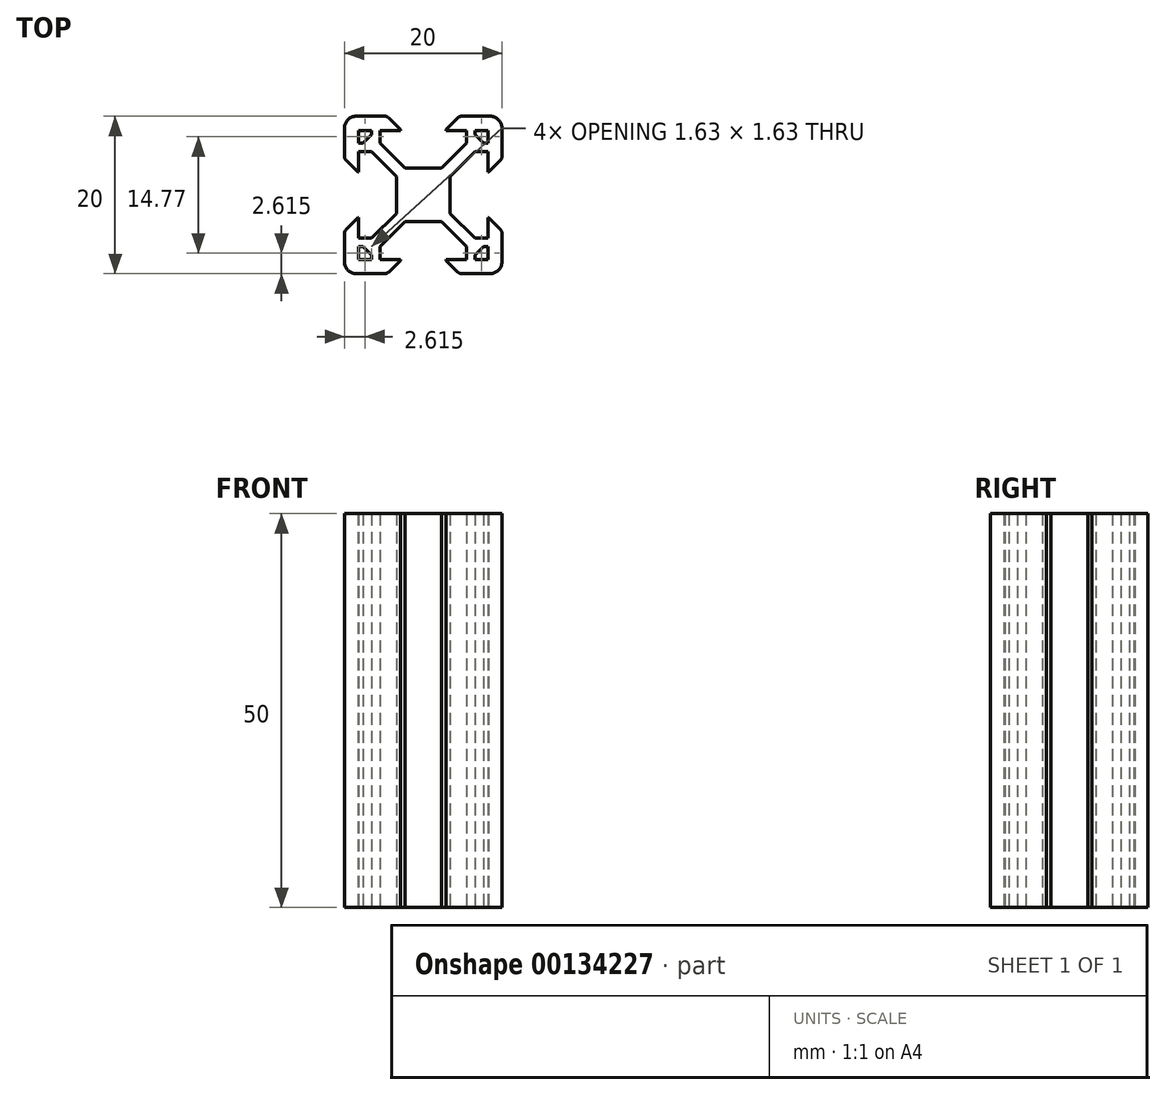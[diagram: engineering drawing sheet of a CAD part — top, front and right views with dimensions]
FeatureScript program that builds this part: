
annotation { "Feature Type Name" : "Feature", "Feature Type Description" : "" }
export const myFeature = defineFeature(function(context is Context, id is Id, definition is map)
    precondition{}
    {
        {
            var Q0;
            Q0=qCreatedBy(makeId("Top.planeOp"),FACE);
            var sketch = newSketch(context, id + "F0", { "sketchPlane" : qUnion([Q0])});
            skLineSegment(sketch, "E0.0.0", {"start": v(-6.56, 5.5) * mm, "end": v(-3.4, 2.34) * mm});
            skLineSegment(sketch, "E0.0.1", {"start": v(-3.4, 2.34) * mm, "end": v(-3.4, -2.34) * mm});
            skLineSegment(sketch, "E0.0.2", {"start": v(-3.4, -2.34) * mm, "end": v(-6.56, -5.5) * mm});
            skLineSegment(sketch, "E0.0.3", {"start": v(-6.56, -5.5) * mm, "end": v(-8.2, -5.5) * mm});
            skLineSegment(sketch, "E0.0.4", {"start": v(-8.2, -5.5) * mm, "end": v(-8.2, -2.9) * mm});
            skLineSegment(sketch, "E0.0.5", {"start": v(-8.2, -2.9) * mm, "end": v(-8.3, -2.9) * mm});
            skLineSegment(sketch, "E0.0.6", {"start": v(-8.3, -2.9) * mm, "end": v(-9.77, -4.35) * mm});
            skArc(sketch, "E0.0.7", {"start": v(-9.77, -4.35) * mm, "mid": v(-9.94, -4.6) * mm, "end": v(-10, -4.9) * mm});
            skLineSegment(sketch, "E0.0.8", {"start": v(-10, -4.9) * mm, "end": v(-10, -8.5) * mm});
            skArc(sketch, "E0.0.9", {"start": v(-10, -8.5) * mm, "mid": v(-9.56, -9.56) * mm, "end": v(-8.5, -10) * mm});
            skLineSegment(sketch, "E0.0.10", {"start": v(-8.5, -10) * mm, "end": v(-4.9, -10) * mm});
            skArc(sketch, "E0.0.11", {"start": v(-4.9, -10) * mm, "mid": v(-4.6, -9.94) * mm, "end": v(-4.35, -9.77) * mm});
            skLineSegment(sketch, "E0.0.12", {"start": v(-4.35, -9.77) * mm, "end": v(-2.89, -8.31) * mm});
            skLineSegment(sketch, "E0.0.13", {"start": v(-2.9, -8.3) * mm, "end": v(-2.89, -8.2) * mm});
            skLineSegment(sketch, "E0.0.14", {"start": v(-2.9, -8.2) * mm, "end": v(-5.5, -8.2) * mm});
            skLineSegment(sketch, "E0.0.15", {"start": v(-5.5, -8.2) * mm, "end": v(-5.5, -6.56) * mm});
            skLineSegment(sketch, "E0.0.16", {"start": v(-5.5, -6.56) * mm, "end": v(-2.34, -3.4) * mm});
            skLineSegment(sketch, "E0.0.17", {"start": v(-2.34, -3.4) * mm, "end": v(2.34, -3.4) * mm});
            skLineSegment(sketch, "E0.0.18", {"start": v(2.34, -3.4) * mm, "end": v(5.5, -6.56) * mm});
            skLineSegment(sketch, "E0.0.19", {"start": v(5.5, -6.56) * mm, "end": v(5.5, -8.2) * mm});
            skLineSegment(sketch, "E0.0.20", {"start": v(5.5, -8.2) * mm, "end": v(2.9, -8.2) * mm});
            skLineSegment(sketch, "E0.0.21", {"start": v(2.89, -8.2) * mm, "end": v(2.9, -8.3) * mm});
            skLineSegment(sketch, "E0.0.22", {"start": v(2.89, -8.3) * mm, "end": v(4.35, -9.77) * mm});
            skArc(sketch, "E0.0.23", {"start": v(4.35, -9.77) * mm, "mid": v(4.6, -9.94) * mm, "end": v(4.9, -10) * mm});
            skLineSegment(sketch, "E0.0.24", {"start": v(4.9, -10) * mm, "end": v(8.5, -10) * mm});
            skArc(sketch, "E0.0.25", {"start": v(8.5, -10) * mm, "mid": v(9.56, -9.56) * mm, "end": v(10, -8.5) * mm});
            skLineSegment(sketch, "E0.0.26", {"start": v(10, -8.5) * mm, "end": v(10, -4.9) * mm});
            skArc(sketch, "E0.0.27", {"start": v(10, -4.9) * mm, "mid": v(9.94, -4.6) * mm, "end": v(9.77, -4.35) * mm});
            skLineSegment(sketch, "E0.0.28", {"start": v(9.77, -4.35) * mm, "end": v(8.3, -2.9) * mm});
            skLineSegment(sketch, "E0.0.29", {"start": v(8.3, -2.9) * mm, "end": v(8.2, -2.9) * mm});
            skLineSegment(sketch, "E0.0.30", {"start": v(8.2, -2.9) * mm, "end": v(8.2, -5.5) * mm});
            skLineSegment(sketch, "E0.0.31", {"start": v(8.2, -5.5) * mm, "end": v(6.56, -5.5) * mm});
            skLineSegment(sketch, "E0.0.32", {"start": v(6.56, -5.5) * mm, "end": v(3.4, -2.34) * mm});
            skLineSegment(sketch, "E0.0.33", {"start": v(3.4, -2.34) * mm, "end": v(3.4, 2.34) * mm});
            skLineSegment(sketch, "E0.0.34", {"start": v(3.4, 2.34) * mm, "end": v(6.56, 5.5) * mm});
            skLineSegment(sketch, "E0.0.35", {"start": v(6.56, 5.5) * mm, "end": v(8.2, 5.5) * mm});
            skLineSegment(sketch, "E0.0.36", {"start": v(8.2, 5.5) * mm, "end": v(8.2, 2.9) * mm});
            skLineSegment(sketch, "E0.0.37", {"start": v(8.2, 2.9) * mm, "end": v(8.3, 2.9) * mm});
            skLineSegment(sketch, "E0.0.38", {"start": v(8.3, 2.9) * mm, "end": v(9.77, 4.35) * mm});
            skArc(sketch, "E0.0.39", {"start": v(9.77, 4.35) * mm, "mid": v(9.94, 4.6) * mm, "end": v(10, 4.9) * mm});
            skLineSegment(sketch, "E0.0.40", {"start": v(10, 4.9) * mm, "end": v(10, 8.5) * mm});
            skArc(sketch, "E0.0.41", {"start": v(10, 8.5) * mm, "mid": v(9.56, 9.56) * mm, "end": v(8.5, 10) * mm});
            skLineSegment(sketch, "E0.0.42", {"start": v(8.5, 10) * mm, "end": v(4.9, 10) * mm});
            skArc(sketch, "E0.0.43", {"start": v(4.9, 10) * mm, "mid": v(4.6, 9.94) * mm, "end": v(4.35, 9.77) * mm});
            skLineSegment(sketch, "E0.0.44", {"start": v(4.35, 9.77) * mm, "end": v(2.89, 8.3) * mm});
            skLineSegment(sketch, "E0.0.45", {"start": v(2.9, 8.3) * mm, "end": v(2.89, 8.2) * mm});
            skLineSegment(sketch, "E0.0.46", {"start": v(2.9, 8.2) * mm, "end": v(5.5, 8.2) * mm});
            skLineSegment(sketch, "E0.0.47", {"start": v(5.5, 8.2) * mm, "end": v(5.5, 6.56) * mm});
            skLineSegment(sketch, "E0.0.48", {"start": v(5.5, 6.56) * mm, "end": v(2.34, 3.4) * mm});
            skLineSegment(sketch, "E0.0.49", {"start": v(2.34, 3.4) * mm, "end": v(-2.34, 3.4) * mm});
            skLineSegment(sketch, "E0.0.50", {"start": v(-2.34, 3.4) * mm, "end": v(-5.5, 6.56) * mm});
            skLineSegment(sketch, "E0.0.51", {"start": v(-5.5, 6.56) * mm, "end": v(-5.5, 8.2) * mm});
            skLineSegment(sketch, "E0.0.52", {"start": v(-5.5, 8.2) * mm, "end": v(-2.9, 8.2) * mm});
            skLineSegment(sketch, "E0.0.53", {"start": v(-2.89, 8.2) * mm, "end": v(-2.9, 8.3) * mm});
            skLineSegment(sketch, "E0.0.54", {"start": v(-2.89, 8.31) * mm, "end": v(-4.35, 9.77) * mm});
            skArc(sketch, "E0.0.55", {"start": v(-4.35, 9.77) * mm, "mid": v(-4.6, 9.94) * mm, "end": v(-4.9, 10) * mm});
            skLineSegment(sketch, "E0.0.56", {"start": v(-4.9, 10) * mm, "end": v(-8.5, 10) * mm});
            skArc(sketch, "E0.0.57", {"start": v(-8.5, 10) * mm, "mid": v(-9.56, 9.56) * mm, "end": v(-10, 8.5) * mm});
            skLineSegment(sketch, "E0.0.58", {"start": v(-10, 8.5) * mm, "end": v(-10, 4.9) * mm});
            skArc(sketch, "E0.0.59", {"start": v(-10, 4.9) * mm, "mid": v(-9.94, 4.6) * mm, "end": v(-9.77, 4.35) * mm});
            skLineSegment(sketch, "E0.0.60", {"start": v(-9.77, 4.35) * mm, "end": v(-8.3, 2.9) * mm});
            skLineSegment(sketch, "E0.0.61", {"start": v(-8.3, 2.9) * mm, "end": v(-8.2, 2.9) * mm});
            skLineSegment(sketch, "E0.0.62", {"start": v(-8.2, 2.9) * mm, "end": v(-8.2, 5.5) * mm});
            skLineSegment(sketch, "E0.0.63", {"start": v(-8.2, 5.5) * mm, "end": v(-6.56, 5.5) * mm});
            skLineSegment(sketch, "E1.0", {"start": v(-6.57, 8.2) * mm, "end": v(-8.2, 8.2) * mm});
            skLineSegment(sketch, "E2.0", {"start": v(-8.2, 8.2) * mm, "end": v(-8.2, 6.57) * mm});
            skLineSegment(sketch, "E3.0", {"start": v(-6.57, 7.66) * mm, "end": v(-6.57, 8.2) * mm});
            skLineSegment(sketch, "E4.0", {"start": v(-7.66, 6.57) * mm, "end": v(-6.57, 7.66) * mm});
            skLineSegment(sketch, "E5.0", {"start": v(-8.2, 6.57) * mm, "end": v(-7.66, 6.57) * mm});
            skLineSegment(sketch, "E6.1.0", {"start": v(-6.57, -7.66) * mm, "end": v(-7.66, -6.57) * mm});
            skLineSegment(sketch, "E6.1.1", {"start": v(-8.2, -6.57) * mm, "end": v(-8.2, -8.2) * mm});
            skLineSegment(sketch, "E6.1.2", {"start": v(-8.2, -8.2) * mm, "end": v(-6.57, -8.2) * mm});
            skLineSegment(sketch, "E6.1.3", {"start": v(-7.66, -6.57) * mm, "end": v(-8.2, -6.57) * mm});
            skLineSegment(sketch, "E6.1.4", {"start": v(-6.57, -8.2) * mm, "end": v(-6.57, -7.66) * mm});
            skLineSegment(sketch, "E6.2.0", {"start": v(7.66, -6.57) * mm, "end": v(6.57, -7.66) * mm});
            skLineSegment(sketch, "E6.2.1", {"start": v(6.57, -8.2) * mm, "end": v(8.2, -8.2) * mm});
            skLineSegment(sketch, "E6.2.2", {"start": v(8.2, -8.2) * mm, "end": v(8.2, -6.57) * mm});
            skLineSegment(sketch, "E6.2.3", {"start": v(6.57, -7.66) * mm, "end": v(6.57, -8.2) * mm});
            skLineSegment(sketch, "E6.2.4", {"start": v(8.2, -6.57) * mm, "end": v(7.66, -6.57) * mm});
            skLineSegment(sketch, "E6.3.0", {"start": v(6.57, 7.66) * mm, "end": v(7.66, 6.57) * mm});
            skLineSegment(sketch, "E6.3.1", {"start": v(8.2, 6.57) * mm, "end": v(8.2, 8.2) * mm});
            skLineSegment(sketch, "E6.3.2", {"start": v(8.2, 8.2) * mm, "end": v(6.57, 8.2) * mm});
            skLineSegment(sketch, "E6.3.3", {"start": v(7.66, 6.57) * mm, "end": v(8.2, 6.57) * mm});
            skLineSegment(sketch, "E6.3.4", {"start": v(6.57, 8.2) * mm, "end": v(6.57, 7.66) * mm});
            skPoint(sketch, "E6.center", {"position": v(0, 0) * mm});
            skSolve(sketch);
        }
        {
            var Q0;
            Q0=makeQuery(id+"F0.imprint","IMPRINT",FACE,{"disambiguationData":[TD([[makeQuery(id+"F0.imprint","IMPRINT",EDGE,{"derivedFrom":sQuery(id+"F0.wireOp",EDGE,"E0.0.0")}),1.0]])]});
            extrude(context, id + "F1", {"entities" : qUnion([Q0]), "endBound" : BoundingType.SYMMETRIC, "depth" : 50 * mm});
        }
    });
